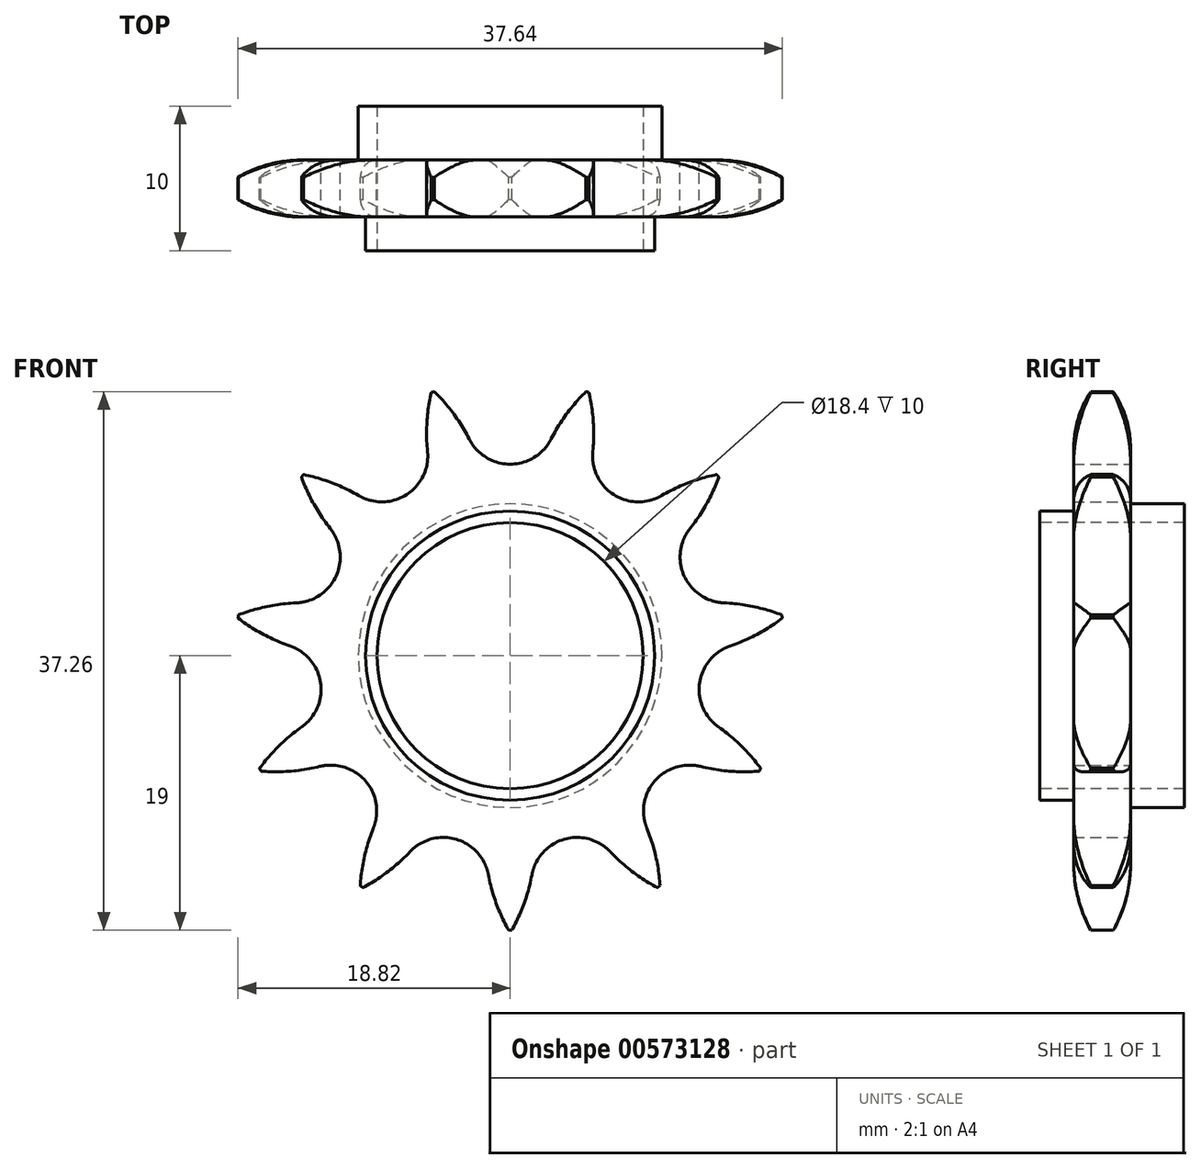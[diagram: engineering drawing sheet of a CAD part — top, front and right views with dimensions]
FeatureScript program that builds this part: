
annotation { "Feature Type Name" : "Feature", "Feature Type Description" : "" }
export const myFeature = defineFeature(function(context is Context, id is Id, definition is map)
    precondition{}
    {
        {
            var Q0;
            Q0=qCreatedBy(makeId("Front.planeOp"),FACE);
            var sketch = newSketch(context, id + "F0", { "sketchPlane" : qUnion([Q0])});
            skCircle(sketch, "E0", {"center": v(0, 0) * mm, "radius": 19 * mm});
            skSolve(sketch);
        }
        {
            var Q0;
            Q0 = qSketchRegion(id + "F0", true);
            extrude(context, id + "F1", {"entities" : qUnion([Q0]), "depth" : 3.94 * mm, "offsetDistance" : 25 * mm, "symmetric" : true});
        }
        {
            var Q0;
            Q0=qCreatedBy(makeId("Front.planeOp"),FACE);
            var sketch = newSketch(context, id + "F2", { "sketchPlane" : qUnion([Q0])});
            skArc(sketch, "E1", {"start": v(-2.83, 14.97) * mm, "mid": v(0, 13.24) * mm, "end": v(2.83, 14.97) * mm});
            skLineSegment(sketch, "E2", {"start": v(-14.06, 9.25) * mm, "end": v(0, 16.42) * mm});
            skLineSegment(sketch, "E3.MirrorCS", {"start": v(14.06, 9.25) * mm, "end": v(0, 16.42) * mm, "construction": true});
            skLineSegment(sketch, "E4.MirrorCS", {"start": v(-14.06, 9.25) * mm, "end": v(0, 16.41) * mm, "construction": true});
            skArc(sketch, "E5", {"start": v(5.25, 18.26) * mm, "mid": v(3.9, 16.72) * mm, "end": v(2.83, 14.97) * mm});
            skArc(sketch, "E6.0", {"start": v(5.25, 18.26) * mm, "mid": v(0, 19) * mm, "end": v(-5.25, 18.26) * mm});
            skArc(sketch, "E7.MirrorCS", {"start": v(-5.25, 18.26) * mm, "mid": v(-3.9, 16.72) * mm, "end": v(-2.83, 14.97) * mm});
            skSolve(sketch);
        }
        {
            var Q0;
            Q0 = qSketchRegion(id + "F2", true);
            extrude(context, id + "F3", {"entities" : qUnion([Q0]), "endBound" : BoundingType.UP_TO_NEXT, "depth" : 25 * mm, "offsetDistance" : 25 * mm, "hasSecondDirection" : true, "secondDirectionBound" : BoundingType.UP_TO_NEXT, "secondDirectionOppositeDirection" : true, "secondDirectionDepth" : 25 * mm});
        }
        {
            var Q0;
            Q0=makeQuery(id+"F3.opExtrude","SWEPT_BODY",BODY,{"disambiguationData":[OSD([sQuery(id+"F2.wireOp",EDGE,"E1"),sQuery(id+"F2.wireOp",EDGE,"E5"),sQuery(id+"F2.wireOp",EDGE,"E6.0"),sQuery(id+"F2.wireOp",EDGE,"E7.MirrorCS")])]});
            var Q1;
            Q1=makeQuery(id+"F1.opExtrude","SWEPT_FACE",FACE,{"disambiguationData":[OSD([sQuery(id+"F0.wireOp",EDGE,"E0")])]});
            circularPattern(context, id + "F4", {"operationType" : NewBodyOperationType.REMOVE, "entities" : qUnion([Q0]), "axis" : qUnion([Q1]), "angle" : 360 * degree, "instanceCount" : 11, "equalSpace" : true});
        }
        {
            var Q0;
            Q0=qCreatedBy(makeId("Right.planeOp"),FACE);
            var sketch = newSketch(context, id + "F5", { "sketchPlane" : qUnion([Q0])});
            skLineSegment(sketch, "E8", {"start": v(-1.97, -14.39) * mm, "end": v(-1.97, -19) * mm});
            skLineSegment(sketch, "E9", {"start": v(-1.97, -19) * mm, "end": v(-0.78, -19) * mm});
            skArc(sketch, "E10", {"start": v(-1.97, -14.39) * mm, "mid": v(-1.67, -16.77) * mm, "end": v(-0.78, -19) * mm});
            skLineSegment(sketch, "E11.0", {"start": v(-1.97, -19) * mm, "end": v(1.97, -19) * mm});
            skLineSegment(sketch, "E12.0", {"start": v(-1.97, -19) * mm, "end": v(-1.97, -15.16) * mm});
            skLineSegment(sketch, "E13.MirrorCS", {"start": v(1.97, -19) * mm, "end": v(1.97, -15.16) * mm});
            skArc(sketch, "E14.MirrorCS", {"start": v(1.97, -14.39) * mm, "mid": v(1.67, -16.77) * mm, "end": v(0.78, -19) * mm});
            skLineSegment(sketch, "E15.MirrorCS", {"start": v(1.97, -14.39) * mm, "end": v(1.97, -19) * mm});
            skSolve(sketch);
        }
        {
            var Q0;
            Q0 = qSketchRegion(id + "F5", true);
            var Q1;
            {var subQ0=sQuery(id+"F0.wireOp",EDGE,"E0");Q1=makeQuery(id+"F4.boolean.opBoolean","SPLIT",FACE,{"disambiguationData":[TD([makeQuery(id+"F4.opPattern","COPY",FACE,{"derivedFrom":makeQuery(id+"F3.opExtrude","SWEPT_FACE",FACE,{"disambiguationData":[OSD([sQuery(id+"F2.wireOp",EDGE,"E5")])]}),"instanceName":"6"})])],"derivedFrom":makeQuery(id+"F1.opExtrude","SWEPT_FACE",FACE,{"disambiguationData":[OSD([subQ0])]})});}
            revolve(context, id + "F6", {"operationType" : NewBodyOperationType.REMOVE, "entities" : qUnion([Q0]), "axis" : qUnion([Q1]), "revolveType" : RevolveType.FULL, "oppositeDirection" : true});
        }
        {
            var Q0;
            Q0=qCreatedBy(makeId("Front.planeOp"),FACE);
            var sketch = newSketch(context, id + "F7", { "sketchPlane" : qUnion([Q0])});
            skCircle(sketch, "E16", {"center": v(0, 0) * mm, "radius": 9.2 * mm});
            skCircle(sketch, "E17", {"center": v(0, 0) * mm, "radius": 10 * mm});
            skCircle(sketch, "E18", {"center": v(0, 0) * mm, "radius": 10.5 * mm});
            skSolve(sketch);
        }
        {
            var Q0;
            Q0=makeQuery(id+"F7.imprint","IMPRINT",FACE,{"disambiguationData":[TD([[makeQuery(id+"F7.imprint","IMPRINT",EDGE,{"derivedFrom":sQuery(id+"F7.wireOp",EDGE,"E16")}),1.0]])]});
            extrude(context, id + "F8", {"entities" : qUnion([Q0]), "operationType" : NewBodyOperationType.REMOVE, "oppositeDirection" : true, "depth" : 25 * mm, "offsetDistance" : 25 * mm, "symmetric" : true});
        }
        {
            var Q0;
            Q0=makeQuery(id+"F7.imprint","IMPRINT",FACE,{"disambiguationData":[TD([[makeQuery(id+"F7.imprint","IMPRINT",EDGE,{"derivedFrom":sQuery(id+"F7.wireOp",EDGE,"E16")}),-1.0]])]});
            extrude(context, id + "F9", {"entities" : qUnion([Q0]), "operationType" : NewBodyOperationType.ADD, "depth" : 4.3 * mm, "offsetDistance" : 25 * mm});
        }
        {
            var Q0;
            Q0=makeQuery(id+"F7.imprint","IMPRINT",FACE,{"disambiguationData":[TD([[makeQuery(id+"F7.imprint","IMPRINT",EDGE,{"derivedFrom":sQuery(id+"F7.wireOp",EDGE,"E17")}),-1.0]])]});
            var Q1;
            Q1=makeQuery(id+"F7.imprint","IMPRINT",FACE,{"disambiguationData":[TD([[makeQuery(id+"F7.imprint","IMPRINT",EDGE,{"derivedFrom":sQuery(id+"F7.wireOp",EDGE,"E16")}),-1.0]])]});
            extrude(context, id + "F10", {"entities" : qUnion([Q0, Q1]), "operationType" : NewBodyOperationType.ADD, "oppositeDirection" : true, "depth" : (10 - 4.3) * mm, "offsetDistance" : 25 * mm});
        }
    });
